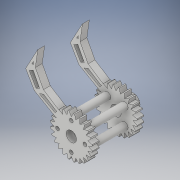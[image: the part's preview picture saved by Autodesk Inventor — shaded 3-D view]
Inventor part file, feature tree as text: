
AUTODESK INVENTOR PART (.ipt)
format: ipt  version: 2017 (Build 210142000, 142)  size: 636,928 bytes
history: native  units: in
note: dims shown in document units (in); Inventor stores cm internally (conversion verified against a paired STEP export)
features: extrude x27, sketch x27
ambient origin geometry x8: Origin, YZ Plane, XZ Plane, XY Plane, X Axis, Y Axis, Z Axis, Center Point
bodies: Solid1 (feature_tree)
feature tree (54):
  extrude  "Extrusion1"  Depth=0.5in
  extrude  "Extrusion2"  TaperAngle=150.0deg  [1 undecoded]
  extrude  "Extrusion3"  Depth=0.2in TaperAngle=0.0deg
  extrude  "Extrusion4"  TaperAngle=30.0deg  [1 undecoded]
  extrude  "Extrusion5"  TaperAngle=60.0deg  [1 undecoded]
  extrude  "Extrusion6"  Depth=0.2in TaperAngle=0.0deg
  extrude  "Extrusion7"  Depth=0.2in
  extrude  "Extrusion8"  Depth=0.2in TaperAngle=0.0deg
  extrude  "Extrusion9"  Depth=0.2in TaperAngle=0.0deg
  extrude  "Extrusion10"  Depth=0.4in
  extrude  "Extrusion11"  Depth=0.4in
  extrude  "Extrusion12"  Depth=0.4in
  extrude  "Extrusion13"  Depth=0.4in
  extrude  "Extrusion14"  Depth=0.2in TaperAngle=0.0deg
  extrude  "Extrusion15"  TaperAngle=60.0deg  [1 undecoded]
  extrude  "Extrusion16"  Depth=0.5in
  extrude  "Extrusion17"  Depth=0.2in TaperAngle=0.0deg
  extrude  "Extrusion18"  TaperAngle=135.0deg  [1 undecoded]
  extrude  "Extrusion19"  TaperAngle=45.0deg  [1 undecoded]
  extrude  "Extrusion20"  TaperAngle=135.0deg  [1 undecoded]
  extrude  "Extrusion21"  Depth=0.2in
  extrude  "Extrusion22"  Depth=1.1in TaperAngle=0.0deg
  extrude  "Extrusion23"  Depth=0.2in TaperAngle=0.0deg
  extrude  "Extrusion24"  Depth=0.2in TaperAngle=0.0deg
  extrude  "Extrusion25"  Depth=0.2in TaperAngle=0.0deg
  extrude  "Extrusion26"  Depth=0.2in TaperAngle=0.0deg
  extrude  "Extrusion27"  Depth=0.2in TaperAngle=0.0deg
  sketch  "Sketch1"  dims[d0=0.5in d1=0.5in]
  sketch  "Sketch2"  dims[d2=15.0deg d3=150.0deg]
  sketch  "Sketch3"  dims[d4=30.0deg d5=0.2in d6=0.0in]
  sketch  "Sketch4"  dims[d7=0.5in d8=30.0deg]
  sketch  "Sketch5"  dims[d9=60.0deg d10=60.0deg]
  sketch  "Sketch6"  dims[d11=0.2in d12=0.0in d13=0.2in d14=0.0in]
  sketch  "Sketch7"  dims[d15=0.2in d16=0.0in d17=1.0in]
  sketch  "Sketch8"  dims[d18=0.2in d19=0.0in d20=0.2in d21=0.0in]
  sketch  "Sketch9"  dims[d22=0.3in d23=0.2in d24=0.0in]
  sketch  "Sketch10"  dims[d25=0.2in d26=0.0in d27=0.4in]
  sketch  "Sketch11"  dims[d28=0.11in d29=0.4in]
  sketch  "Sketch12"  dims[d30=0.11in d31=0.4in]
  sketch  "Sketch13"  dims[d32=0.4in d33=0.11in]
  sketch  "Sketch14"  dims[d34=0.11in d35=0.2in d36=0.0in]
  sketch  "Sketch15"  dims[d37=1.5in d38=60.0deg]
  sketch  "Sketch16"  dims[d39=30.0deg d40=0.5in]
  sketch  "Sketch17"  dims[d41=150.0deg d42=0.2in d43=0.0in]
  sketch  "Sketch18"  dims[d44=0.2in d45=0.0in d46=135.0deg]
  sketch  "Sketch19"  dims[d47=0.2in d48=45.0deg]
  sketch  "Sketch20"  dims[d49=45.0deg d50=135.0deg]
  sketch  "Sketch21"  dims[d51=0.2in d52=0.2in]
  sketch  "Sketch22"  dims[d53=0.2in d54=1.1in d55=0.0in]
  sketch  "Sketch23"  dims[d56=30.0deg d57=0.2in d58=0.0in]
  sketch  "Sketch24"  dims[d59=0.2in d60=0.0in d61=0.2in d62=0.0in]
  sketch  "Sketch25"  dims[d63=0.2in d64=0.0in d65=0.2in d66=0.0in]
  sketch  "Sketch26"  dims[d67=0.2in d68=0.0in d69=0.2in d70=0.0in]
  sketch  "Sketch27"  dims[d71=0.3in d72=0.2in d73=0.0in d74=0.2in d75=0.0in d76=2.0in d77=0.0in d78=2.0in d79=0.0in d80=2.0in d81=0.0in d82=0.6in d83=0.05in d84=0.0in d85=0.4in d86=0.25in d87=0.0in d88=0.3in d89=1.0in d90=0.0in]
note: 7 required parameter values undecoded (feature->parameter linkage not recoverable at this tier; creation-order binding heuristic only, values carry confidence <= 0.55)
